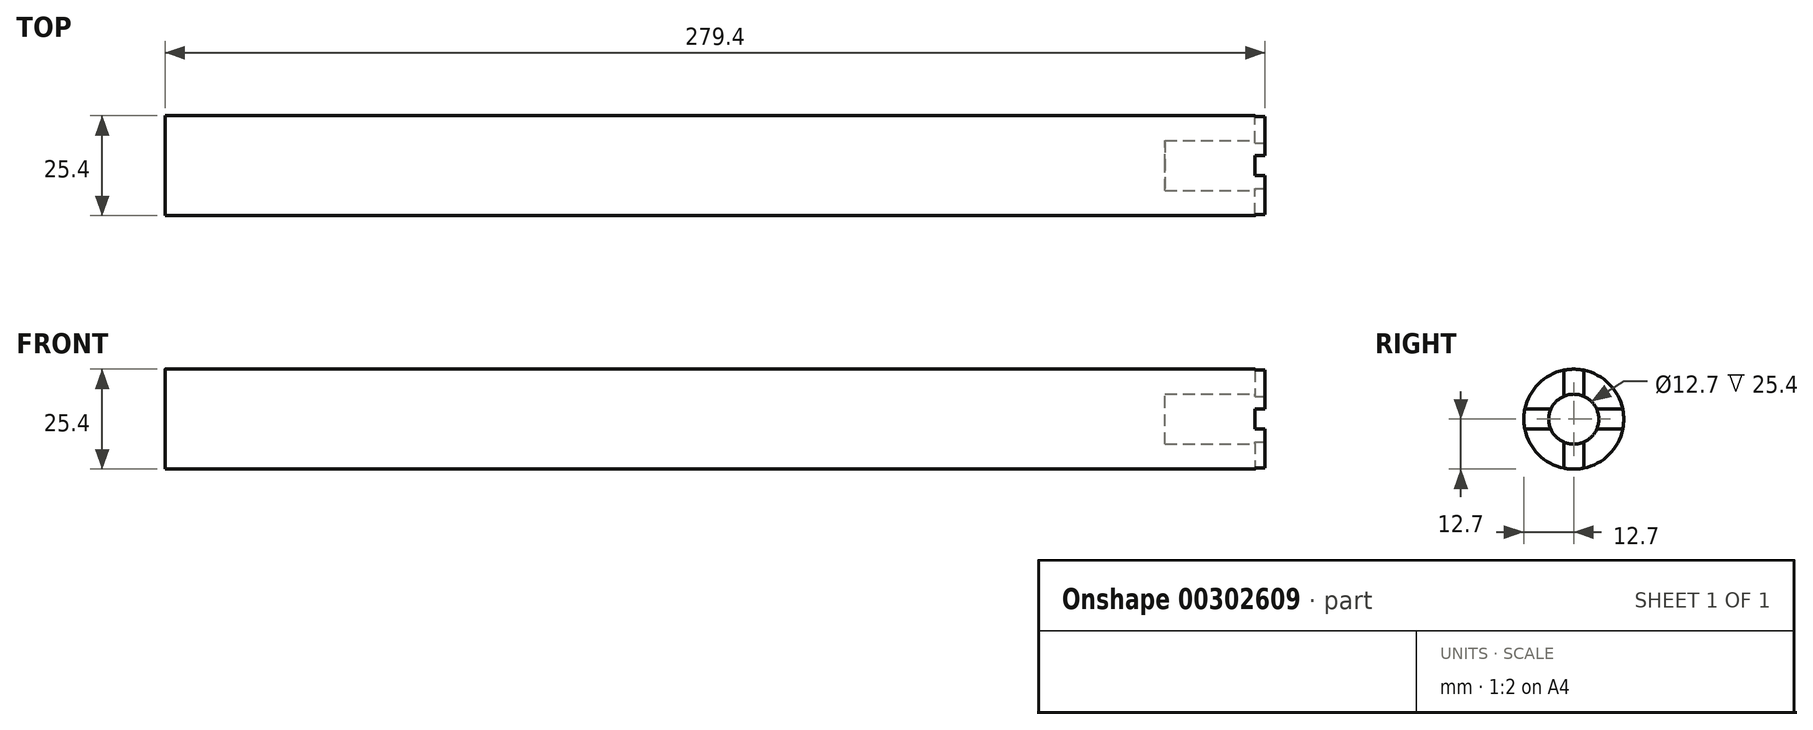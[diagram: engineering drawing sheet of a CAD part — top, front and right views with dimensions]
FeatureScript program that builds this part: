
annotation { "Feature Type Name" : "Feature", "Feature Type Description" : "" }
export const myFeature = defineFeature(function(context is Context, id is Id, definition is map)
    precondition{}
    {
        {
            var Q0;
            Q0=qCreatedBy(makeId("Right.planeOp"),FACE);
            var sketch = newSketch(context, id + "F0", { "sketchPlane" : qUnion([Q0])});
            skCircle(sketch, "E0", {"center": v(0, 0) * mm, "radius": 12.7 * mm});
            skSolve(sketch);
        }
        {
            var Q0;
            Q0 = qSketchRegion(id + "F0", true);
            extrude(context, id + "F1", {"entities" : qUnion([Q0]), "depth" : 279.4 * mm});
        }
        {
            var Q0;
            Q0=makeQuery(id+"F1.opExtrude","CAP_FACE",FACE,{"disambiguationData":[OSD([sQuery(id+"F0.wireOp",EDGE,"E0")])],"isStart":false});
            var sketch = newSketch(context, id + "F2", { "sketchPlane" : qUnion([Q0])});
            skCircle(sketch, "E1", {"center": v(0, 0) * mm, "radius": 6.35 * mm});
            skSolve(sketch);
        }
        {
            var Q0;
            Q0 = qSketchRegion(id + "F2", true);
            extrude(context, id + "F3", {"entities" : qUnion([Q0]), "operationType" : NewBodyOperationType.REMOVE, "oppositeDirection" : true, "depth" : 25.4 * mm});
        }
        {
            var Q0;
            Q0=makeQuery(id+"F1.opExtrude","CAP_FACE",FACE,{"disambiguationData":[OSD([sQuery(id+"F0.wireOp",EDGE,"E0")])],"isStart":false});
            var sketch = newSketch(context, id + "F4", { "sketchPlane" : qUnion([Q0])});
            skLineSegment(sketch, "E2", {"start": v(0, 12.7) * mm, "end": v(0, -12.7) * mm, "construction": true});
            skLineSegment(sketch, "E3", {"start": v(-12.7, 0) * mm, "end": v(12.7, 0) * mm, "construction": true});
            skLineSegment(sketch, "E4", {"start": v(-2.54, 12.44) * mm, "end": v(-2.54, 5.82) * mm});
            skLineSegment(sketch, "E5", {"start": v(2.54, 12.44) * mm, "end": v(2.54, 5.82) * mm});
            skLineSegment(sketch, "E6", {"start": v(5.82, 2.54) * mm, "end": v(12.44, 2.54) * mm});
            skLineSegment(sketch, "E7", {"start": v(5.82, -2.54) * mm, "end": v(12.44, -2.54) * mm});
            skLineSegment(sketch, "E8", {"start": v(-2.54, -5.82) * mm, "end": v(-2.54, -12.44) * mm});
            skLineSegment(sketch, "E9", {"start": v(2.54, -5.82) * mm, "end": v(2.54, -12.44) * mm});
            skLineSegment(sketch, "E10", {"start": v(-12.44, -2.54) * mm, "end": v(-5.82, -2.54) * mm});
            skLineSegment(sketch, "E11", {"start": v(-12.44, 2.54) * mm, "end": v(-5.82, 2.54) * mm});
            skArc(sketch, "E12", {"start": v(-12.44, 2.54) * mm, "mid": v(-12.7, 0) * mm, "end": v(-12.44, -2.54) * mm});
            skArc(sketch, "E13", {"start": v(-5.82, 2.54) * mm, "mid": v(-6.35, 0) * mm, "end": v(-5.82, -2.54) * mm});
            skArc(sketch, "E14", {"start": v(2.54, 12.44) * mm, "mid": v(0, 12.7) * mm, "end": v(-2.54, 12.44) * mm});
            skArc(sketch, "E15", {"start": v(12.44, -2.54) * mm, "mid": v(12.7, 0) * mm, "end": v(12.44, 2.54) * mm});
            skArc(sketch, "E16", {"start": v(-2.54, -12.44) * mm, "mid": v(0, -12.7) * mm, "end": v(2.54, -12.44) * mm});
            skArc(sketch, "E17", {"start": v(5.82, -2.54) * mm, "mid": v(6.35, 0) * mm, "end": v(5.82, 2.54) * mm});
            skArc(sketch, "E18", {"start": v(2.54, 5.82) * mm, "mid": v(0, 6.35) * mm, "end": v(-2.54, 5.82) * mm});
            skArc(sketch, "E19", {"start": v(-2.54, -5.82) * mm, "mid": v(0, -6.35) * mm, "end": v(2.54, -5.82) * mm});
            skSolve(sketch);
        }
        {
            var Q0;
            Q0=makeQuery(id+"F4.imprint","IMPRINT",FACE,{"disambiguationData":[TD([[makeQuery(id+"F4.imprint","IMPRINT",EDGE,{"derivedFrom":sQuery(id+"F4.wireOp",EDGE,"E6")}),-1.0]])]});
            var Q1;
            Q1=makeQuery(id+"F4.imprint","IMPRINT",FACE,{"disambiguationData":[TD([[makeQuery(id+"F4.imprint","IMPRINT",EDGE,{"derivedFrom":sQuery(id+"F4.wireOp",EDGE,"E4")}),1.0]])]});
            var Q2;
            Q2=makeQuery(id+"F4.imprint","IMPRINT",FACE,{"disambiguationData":[TD([[makeQuery(id+"F4.imprint","IMPRINT",EDGE,{"derivedFrom":sQuery(id+"F4.wireOp",EDGE,"E10")}),1.0]])]});
            var Q3;
            Q3=makeQuery(id+"F4.imprint","IMPRINT",FACE,{"disambiguationData":[TD([[makeQuery(id+"F4.imprint","IMPRINT",EDGE,{"derivedFrom":sQuery(id+"F4.wireOp",EDGE,"E8")}),1.0]])]});
            extrude(context, id + "F5", {"entities" : qUnion([Q0, Q1, Q2, Q3]), "operationType" : NewBodyOperationType.REMOVE, "oppositeDirection" : true, "depth" : 2.54 * mm});
        }
    });
